# Revit family: КП-2_Eng
name_source: partatom
category: Duct Accessories
units: mm (PartAtom-declared; Revit-internal decimal feet)

## family parameters
Always vertical = Yes
Cut with Voids When Loaded = No
Part Type = Attaches To
Round Connector Dimension = Use Diameter
Shared = No
Work Plane-Based = No

## types (21) — shared parameters
00_20_Manufacturer = Vents
00_20_Name = Fire-resisting damper
Actuator location (inside) = No
Actuator location (outside) = Yes
Casing Material = Metal, painted, blue, matte RAL 5007
Frequency = 50 Hz
Length = 350 mm  [stored 1.14829 ft]
Load Classification = HVAC
Maintenance zone material = <By Category>
Manufacturer = Vents
Maximum Air Flow = 0 m³/h
Number of Fase = 1
Two flanges = Yes
URL = https://ventilation-system.com
Voltage = 230 V
zero-valued in all types: Default Elevation

## per-type parameters (varying)
| type | A | A1 | A2 | A3 | An | Apparent Load | B | B1 | B2 | B3 | Bn | Height | Weight | Width |
| KP-2-200х200-2-PVP230T-SN-1 | 200 mm  [stored 0.656168 ft] | 220 mm  [stored 0.721785 ft] | 240 mm  [stored 0.787402 ft] | 100 mm  [stored 0.328084 ft] | 210 mm  [stored 0.688976 ft] | 7 VA | 200 mm  [stored 0.656168 ft] | 220 mm  [stored 0.721785 ft] | 240 mm  [stored 0.787402 ft] | 110 mm  [stored 0.360892 ft] | 210 mm  [stored 0.688976 ft] | 240 mm  [stored 0.787402 ft] | 5.70 kg | 240 mm  [stored 0.787402 ft] |
| KP-2-1000х1000-2-PVP230T-SN-1 | 1000 mm | 1030 mm | 1060 mm | 500 mm  [stored 1.64042 ft] | 1010 mm | 11 VA | 1000 mm | 1030 mm | 1060 mm | 515 mm  [stored 1.68963 ft] | 1010 mm | 1060 mm | 58.00 kg | 1060 mm |
| KP-2-250х200-2-PVP230T-SN-1 | 250 mm  [stored 0.82021 ft] | 270 mm  [stored 0.885827 ft] | 290 mm  [stored 0.951444 ft] | 125 mm  [stored 0.410105 ft] | 260 mm  [stored 0.853018 ft] | 10 VA | 200 mm  [stored 0.656168 ft] | 220 mm  [stored 0.721785 ft] | 240 mm  [stored 0.787402 ft] | 110 mm  [stored 0.360892 ft] | 210 mm  [stored 0.688976 ft] | 290 mm  [stored 0.951444 ft] | 6.20 kg | 240 mm  [stored 0.787402 ft] |
| KP-2-250х250-2-PVP230T-SN-1 | 250 mm  [stored 0.82021 ft] | 270 mm  [stored 0.885827 ft] | 290 mm  [stored 0.951444 ft] | 125 mm  [stored 0.410105 ft] | 260 mm  [stored 0.853018 ft] | 10 VA | 250 mm  [stored 0.82021 ft] | 270 mm  [stored 0.885827 ft] | 290 mm  [stored 0.951444 ft] | 135 mm  [stored 0.442913 ft] | 260 mm  [stored 0.853018 ft] | 290 mm  [stored 0.951444 ft] | 6.90 kg | 290 mm  [stored 0.951444 ft] |
| KP-2-300х200-2-PVP230T-SN-1 | 300 mm | 320 mm  [stored 1.04987 ft] | 340 mm  [stored 1.11549 ft] | 150 mm | 310 mm  [stored 1.01706 ft] | 10 VA | 200 mm  [stored 0.656168 ft] | 220 mm  [stored 0.721785 ft] | 240 mm  [stored 0.787402 ft] | 110 mm  [stored 0.360892 ft] | 210 mm  [stored 0.688976 ft] | 340 mm  [stored 1.11549 ft] | 6.80 kg | 240 mm  [stored 0.787402 ft] |
| KP-2-300х250-2-PVP230T-SN-1 | 300 mm | 320 mm  [stored 1.04987 ft] | 340 mm  [stored 1.11549 ft] | 150 mm | 310 mm  [stored 1.01706 ft] | 10 VA | 250 mm  [stored 0.82021 ft] | 270 mm  [stored 0.885827 ft] | 290 mm  [stored 0.951444 ft] | 135 mm  [stored 0.442913 ft] | 260 mm  [stored 0.853018 ft] | 340 mm  [stored 1.11549 ft] | 7.50 kg | 290 mm  [stored 0.951444 ft] |
| KP-2-300х300-2-PVP230T-SN-1 | 300 mm | 320 mm  [stored 1.04987 ft] | 340 mm  [stored 1.11549 ft] | 150 mm | 310 mm  [stored 1.01706 ft] | 10 VA | 300 mm | 320 mm  [stored 1.04987 ft] | 340 mm  [stored 1.11549 ft] | 160 mm  [stored 0.524934 ft] | 310 mm  [stored 1.01706 ft] | 340 mm  [stored 1.11549 ft] | 9.20 kg | 340 mm  [stored 1.11549 ft] |
| KP-2-400х250-2-PVP230T-SN-1 | 400 mm  [stored 1.31234 ft] | 420 mm  [stored 1.37795 ft] | 440 mm  [stored 1.44357 ft] | 200 mm  [stored 0.656168 ft] | 410 mm  [stored 1.34514 ft] | 10 VA | 250 mm  [stored 0.82021 ft] | 270 mm  [stored 0.885827 ft] | 290 mm  [stored 0.951444 ft] | 135 mm  [stored 0.442913 ft] | 260 mm  [stored 0.853018 ft] | 440 mm  [stored 1.44357 ft] | 9.00 kg | 290 mm  [stored 0.951444 ft] |
| KP-2-400х300-2-PVP230T-SN-1 | 400 mm  [stored 1.31234 ft] | 420 mm  [stored 1.37795 ft] | 440 mm  [stored 1.44357 ft] | 200 mm  [stored 0.656168 ft] | 410 mm  [stored 1.34514 ft] | 10 VA | 300 mm | 320 mm  [stored 1.04987 ft] | 340 mm  [stored 1.11549 ft] | 160 mm  [stored 0.524934 ft] | 310 mm  [stored 1.01706 ft] | 440 mm  [stored 1.44357 ft] | 10.80 kg | 340 mm  [stored 1.11549 ft] |
| KP-2-400х400-2-PVP230T-SN-1 | 400 mm  [stored 1.31234 ft] | 420 mm  [stored 1.37795 ft] | 440 mm  [stored 1.44357 ft] | 200 mm  [stored 0.656168 ft] | 410 mm  [stored 1.34514 ft] | 10 VA | 400 mm  [stored 1.31234 ft] | 420 mm  [stored 1.37795 ft] | 440 mm  [stored 1.44357 ft] | 210 mm  [stored 0.688976 ft] | 410 mm  [stored 1.34514 ft] | 440 mm  [stored 1.44357 ft] | 12.60 kg | 440 mm  [stored 1.44357 ft] |
| KP-2-500х300-2-PVP230T-SN-1 | 500 mm  [stored 1.64042 ft] | 520 mm  [stored 1.70604 ft] | 540 mm  [stored 1.77165 ft] | 250 mm  [stored 0.82021 ft] | 510 mm  [stored 1.67323 ft] | 10 VA | 300 mm | 320 mm  [stored 1.04987 ft] | 340 mm  [stored 1.11549 ft] | 160 mm  [stored 0.524934 ft] | 310 mm  [stored 1.01706 ft] | 540 mm  [stored 1.77165 ft] | 12.30 kg | 340 mm  [stored 1.11549 ft] |
| KP-2-500х400-2-PVP230T-SN-1 | 500 mm  [stored 1.64042 ft] | 520 mm  [stored 1.70604 ft] | 540 mm  [stored 1.77165 ft] | 250 mm  [stored 0.82021 ft] | 510 mm  [stored 1.67323 ft] | 10 VA | 400 mm  [stored 1.31234 ft] | 420 mm  [stored 1.37795 ft] | 440 mm  [stored 1.44357 ft] | 210 mm  [stored 0.688976 ft] | 410 mm  [stored 1.34514 ft] | 540 mm  [stored 1.77165 ft] | 14.30 kg | 440 mm  [stored 1.44357 ft] |
| KP-2-500х500-2-PVP230T-SN-1 | 500 mm  [stored 1.64042 ft] | 530 mm  [stored 1.73885 ft] | 560 mm  [stored 1.83727 ft] | 250 mm  [stored 0.82021 ft] | 510 mm  [stored 1.67323 ft] | 10 VA | 500 mm  [stored 1.64042 ft] | 530 mm  [stored 1.73885 ft] | 560 mm  [stored 1.83727 ft] | 265 mm  [stored 0.869423 ft] | 510 mm  [stored 1.67323 ft] | 560 mm  [stored 1.83727 ft] | 23.00 kg | 560 mm  [stored 1.83727 ft] |
| KP-2-600х400-2-PVP230T-SN-1 | 600 mm  [stored 1.9685 ft] | 620 mm  [stored 2.03412 ft] | 640 mm  [stored 2.09974 ft] | 300 mm | 610 mm  [stored 2.00131 ft] | 10 VA | 400 mm  [stored 1.31234 ft] | 420 mm  [stored 1.37795 ft] | 440 mm  [stored 1.44357 ft] | 210 mm  [stored 0.688976 ft] | 410 mm  [stored 1.34514 ft] | 640 mm  [stored 2.09974 ft] | 16.20 kg | 440 mm  [stored 1.44357 ft] |
| KP-2-600х500-2-PVP230T-SN-1 | 600 mm  [stored 1.9685 ft] | 630 mm  [stored 2.06693 ft] | 660 mm  [stored 2.16535 ft] | 300 mm | 610 mm  [stored 2.00131 ft] | 11 VA | 500 mm  [stored 1.64042 ft] | 530 mm  [stored 1.73885 ft] | 560 mm  [stored 1.83727 ft] | 265 mm  [stored 0.869423 ft] | 510 mm  [stored 1.67323 ft] | 660 mm  [stored 2.16535 ft] | 25.60 kg | 560 mm  [stored 1.83727 ft] |
| KP-2-600х600-2-PVP230T-SN-1 | 600 mm  [stored 1.9685 ft] | 630 mm  [stored 2.06693 ft] | 660 mm  [stored 2.16535 ft] | 300 mm | 610 mm  [stored 2.00131 ft] | 11 VA | 600 mm  [stored 1.9685 ft] | 630 mm  [stored 2.06693 ft] | 660 mm  [stored 2.16535 ft] | 315 mm  [stored 1.03346 ft] | 610 mm  [stored 2.00131 ft] | 660 mm  [stored 2.16535 ft] | 28.60 kg | 660 mm  [stored 2.16535 ft] |
| KP-2-800х500-2-PVP230T-SN-1 | 800 mm | 830 mm | 860 mm | 400 mm  [stored 1.31234 ft] | 810 mm | 11 VA | 500 mm  [stored 1.64042 ft] | 530 mm  [stored 1.73885 ft] | 560 mm  [stored 1.83727 ft] | 265 mm  [stored 0.869423 ft] | 510 mm  [stored 1.67323 ft] | 860 mm | 31.30 kg | 560 mm  [stored 1.83727 ft] |
| KP-2-800х600-2-PVP230T-SN-1 | 800 mm | 830 mm | 860 mm | 400 mm  [stored 1.31234 ft] | 810 mm | 11 VA | 600 mm  [stored 1.9685 ft] | 630 mm  [stored 2.06693 ft] | 660 mm  [stored 2.16535 ft] | 315 mm  [stored 1.03346 ft] | 610 mm  [stored 2.00131 ft] | 860 mm | 34.70 kg | 660 mm  [stored 2.16535 ft] |
| KP-2-800х800-2-PVP230T-SN-1 | 800 mm | 830 mm | 860 mm | 400 mm  [stored 1.31234 ft] | 810 mm | 11 VA | 800 mm | 830 mm | 860 mm | 415 mm  [stored 1.36155 ft] | 810 mm | 860 mm | 42.00 kg | 860 mm |
| KP-2-1000х600-2-PVP230T-SN-1 | 1000 mm | 1030 mm | 1060 mm | 500 mm  [stored 1.64042 ft] | 1010 mm | 11 VA | 600 mm  [stored 1.9685 ft] | 630 mm  [stored 2.06693 ft] | 660 mm  [stored 2.16535 ft] | 315 mm  [stored 1.03346 ft] | 610 mm  [stored 2.00131 ft] | 1060 mm | 40.70 kg | 660 mm  [stored 2.16535 ft] |
| KP-2-1000х800-2-PVP230T-SN-1 | 1000 mm | 1030 mm | 1060 mm | 500 mm  [stored 1.64042 ft] | 1010 mm | 11 VA | 800 mm | 830 mm | 860 mm | 415 mm  [stored 1.36155 ft] | 810 mm | 1060 mm | 50.20 kg | 860 mm |

note: column(s) folded — value = type name in every type: 00_20_Type

note: [stored X ft] marks values corroborated as IEEE doubles in the binary element streams (Revit-internal decimal feet)

## geometry (parser evidence)
native form markers: Blend x2
no freeform markers — native parametric forms only
